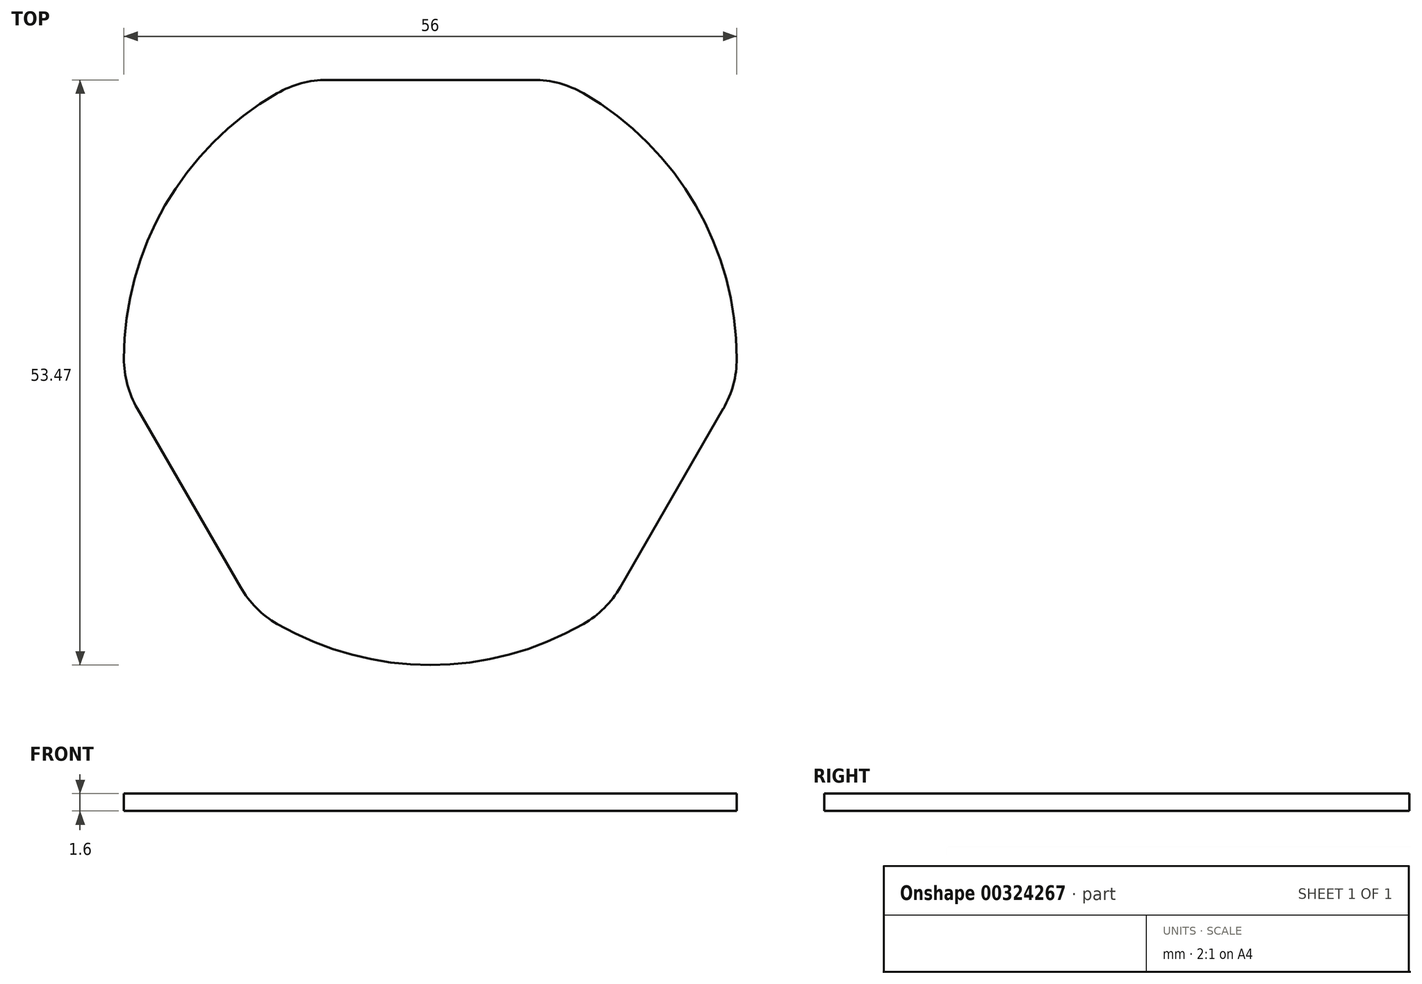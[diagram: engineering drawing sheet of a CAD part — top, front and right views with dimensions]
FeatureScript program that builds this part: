
annotation { "Feature Type Name" : "Feature", "Feature Type Description" : "" }
export const myFeature = defineFeature(function(context is Context, id is Id, definition is map)
    precondition{}
    {
        {
            var Q0;
            Q0=qCreatedBy(makeId("Top.planeOp"),FACE);
            var sketch = newSketch(context, id + "F0", { "sketchPlane" : qUnion([Q0])});
            skCircle(sketch, "E0", {"center": v(0, 0) * mm, "radius": 9.15 * mm, "construction": true});
            skCircle(sketch, "E1", {"center": v(9.42, 16.32) * mm, "radius": 9.15 * mm, "construction": true});
            skCircle(sketch, "E2", {"center": v(-9.42, 16.32) * mm, "radius": 9.15 * mm, "construction": true});
            skCircle(sketch, "E3", {"center": v(-18.85, 0) * mm, "radius": 9.15 * mm, "construction": true});
            skCircle(sketch, "E4", {"center": v(-9.42, -16.32) * mm, "radius": 9.15 * mm, "construction": true});
            skCircle(sketch, "E5", {"center": v(9.42, -16.32) * mm, "radius": 9.15 * mm, "construction": true});
            skCircle(sketch, "E6", {"center": v(18.85, 0) * mm, "radius": 9.15 * mm, "construction": true});
            skLineSegment(sketch, "E7", {"start": v(-9.42, 16.32) * mm, "end": v(0, 0) * mm, "construction": true});
            skLineSegment(sketch, "E8", {"start": v(9.42, 16.32) * mm, "end": v(0, 0) * mm, "construction": true});
            skLineSegment(sketch, "E9", {"start": v(18.85, 0) * mm, "end": v(0, 0) * mm, "construction": true});
            skLineSegment(sketch, "E10", {"start": v(9.42, -16.32) * mm, "end": v(0, 0) * mm, "construction": true});
            skLineSegment(sketch, "E11", {"start": v(0, 0) * mm, "end": v(-9.42, -16.32) * mm, "construction": true});
            skLineSegment(sketch, "E12", {"start": v(-18.85, 0) * mm, "end": v(0, 0) * mm, "construction": true});
            skLineSegment(sketch, "E13", {"start": v(-18.85, 0) * mm, "end": v(-9.42, 16.32) * mm, "construction": true});
            skLineSegment(sketch, "E14", {"start": v(-9.42, 16.32) * mm, "end": v(9.42, 16.32) * mm, "construction": true});
            skLineSegment(sketch, "E15", {"start": v(9.42, 16.32) * mm, "end": v(18.85, 0) * mm, "construction": true});
            skLineSegment(sketch, "E16", {"start": v(18.85, 0) * mm, "end": v(9.42, -16.32) * mm, "construction": true});
            skLineSegment(sketch, "E17", {"start": v(9.42, -16.32) * mm, "end": v(-9.42, -16.32) * mm, "construction": true});
            skLineSegment(sketch, "E18", {"start": v(-9.42, -16.32) * mm, "end": v(-18.85, 0) * mm, "construction": true});
            skArc(sketch, "E19", {"start": v(-14, 24.25) * mm, "mid": v(-24.25, 14) * mm, "end": v(-28, 0) * mm});
            skLineSegment(sketch, "E20", {"start": v(-9.42, 25.47) * mm, "end": v(9.42, 25.47) * mm});
            skArc(sketch, "E21", {"start": v(-14, 24.25) * mm, "mid": v(-11.8, 25.16) * mm, "end": v(-9.42, 25.47) * mm});
            skArc(sketch, "E22", {"start": v(9.42, 25.47) * mm, "mid": v(11.8, 25.16) * mm, "end": v(14, 24.25) * mm});
            skLineSegment(sketch, "E23", {"start": v(-26.77, -4.57) * mm, "end": v(-17.35, -20.9) * mm});
            skLineSegment(sketch, "E24", {"start": v(17.35, -20.9) * mm, "end": v(26.77, -4.57) * mm});
            skArc(sketch, "E25.trimOffspring", {"start": v(28, 0) * mm, "mid": v(24.25, 14) * mm, "end": v(14, 24.25) * mm});
            skArc(sketch, "E26.trimOffspring", {"start": v(-14, -24.25) * mm, "mid": v(0, -28) * mm, "end": v(14, -24.25) * mm});
            skArc(sketch, "E27", {"start": v(-26.77, -4.57) * mm, "mid": v(-27.69, -2.37) * mm, "end": v(-28, 0) * mm});
            skArc(sketch, "E28", {"start": v(-14, -24.25) * mm, "mid": v(-15.9, -22.8) * mm, "end": v(-17.35, -20.9) * mm});
            skArc(sketch, "E29", {"start": v(17.35, -20.9) * mm, "mid": v(15.9, -22.8) * mm, "end": v(14, -24.25) * mm});
            skArc(sketch, "E30", {"start": v(28, 0) * mm, "mid": v(27.69, -2.37) * mm, "end": v(26.77, -4.58) * mm});
            skCircle(sketch, "E31", {"center": v(0, 0) * mm, "radius": 29 * mm, "construction": true});
            skSolve(sketch);
        }
        {
            var Q0;
            Q0 = qSketchRegion(id + "F0", true);
            extrude(context, id + "F1", {"entities" : qUnion([Q0]), "depth" : 1.6 * mm});
        }
    });
